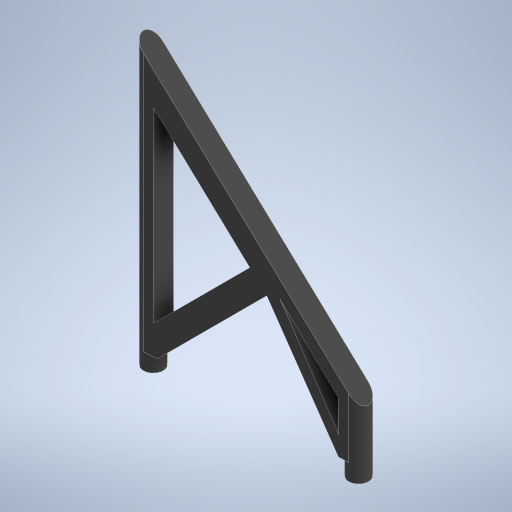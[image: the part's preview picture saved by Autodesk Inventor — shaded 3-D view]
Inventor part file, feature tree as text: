
AUTODESK INVENTOR PART (.ipt)
format: ipt  version: 2024.2 (Build 282272000, 272)  size: 318,976 bytes
history: native  units: mm
features: extrude x4, sketch x4, plane x1
ambient origin geometry x8: Origin, YZ Plane, XZ Plane, XY Plane, X Axis, Y Axis, Z Axis, Center Point
bodies: Solid1 (feature_tree)
feature tree (9):
  extrude  "Extrusion1"  Depth=3.0mm
  extrude  "Extrusion2"  Depth=3.0mm
  plane  "Work Plane1"
  extrude  "Extrusion3"  Depth=1.0mm
  extrude  "Extrusion4"  Depth=51.0mm
  sketch  "Sketch1"  dims[d0=3.0mm d1=3.0mm]
  sketch  "Sketch2"  dims[d2=3.0mm d3=3.0mm]
  sketch  "Sketch3"  dims[d5=49.0mm d6=1.0mm]
  sketch  "Sketch4"  dims[d7=30.0mm d8=51.0mm d9=2.5mm d10=0.0mm d11=45.0mm d12=0.0mm d13=2.0mm d14=45.0deg d15=10.0mm d16=45.0mm d17=0.0mm d18=3.5mm d19=3.5mm d20=3.5mm d21=3.5mm d22=45.0deg d23=3.0mm d24=1.8mm d25=3.0mm d26=2.0mm d27=12.283116mm d28=3.0mm d29=43.0mm d30=10.0mm d31=0.0mm]
